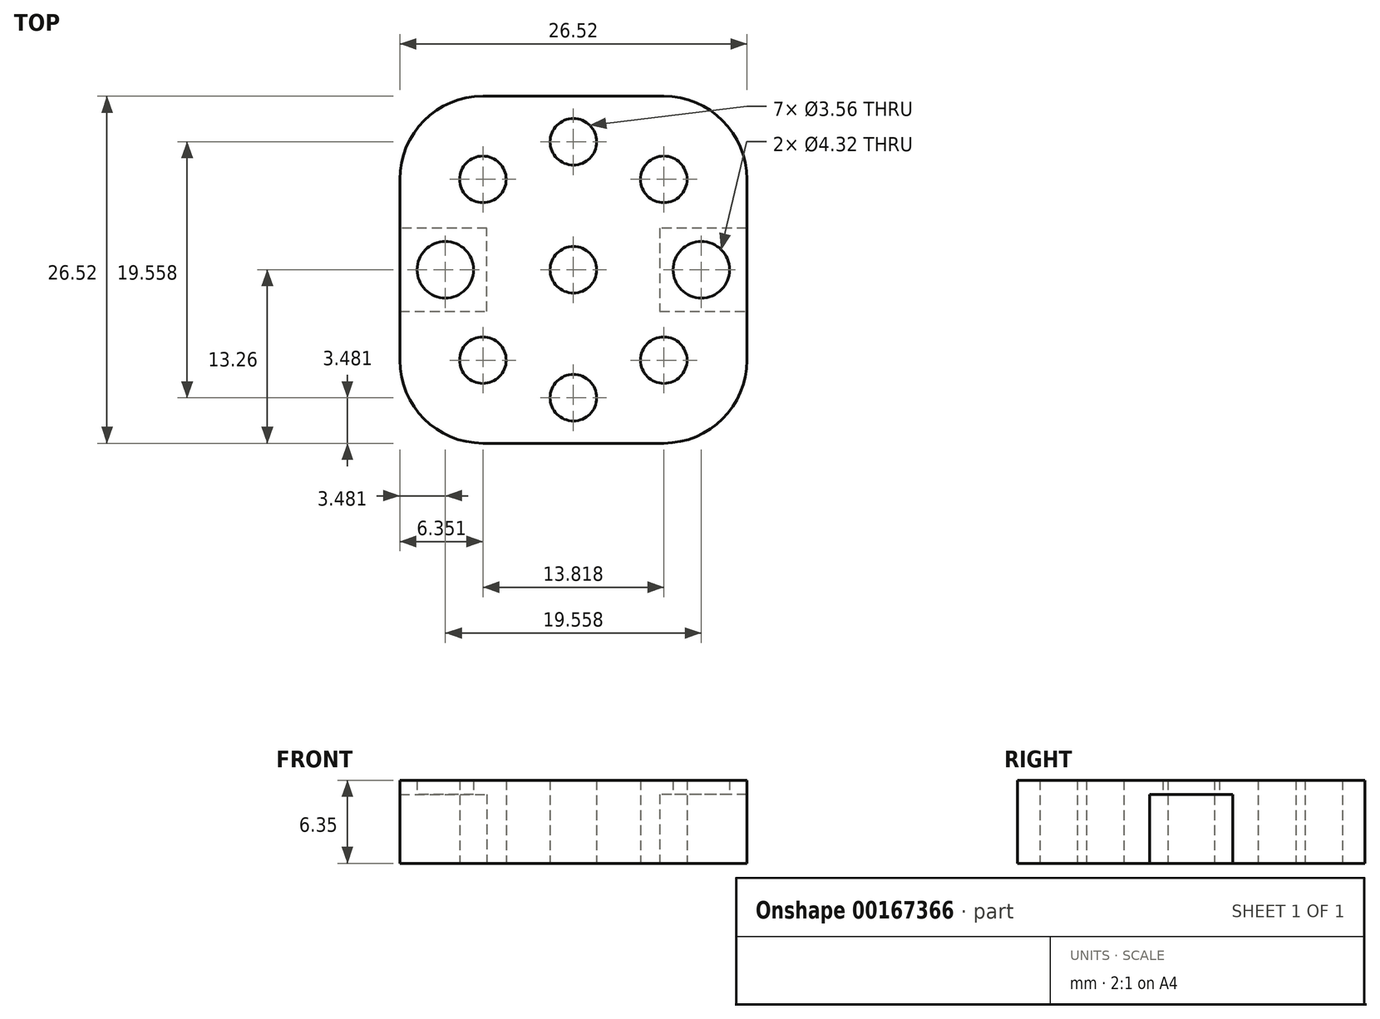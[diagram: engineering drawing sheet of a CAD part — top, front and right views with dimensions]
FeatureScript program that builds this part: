
annotation { "Feature Type Name" : "Feature", "Feature Type Description" : "" }
export const myFeature = defineFeature(function(context is Context, id is Id, definition is map)
    precondition{}
    {
        {
            var Q0;
            Q0=qCreatedBy(makeId("Top.planeOp"),FACE);
            var sketch = newSketch(context, id + "F0", { "sketchPlane" : qUnion([Q0])});
            skLineSegment(sketch, "E0.bottom", {"start": v(6.9, 13.26) * mm, "end": v(-6.9, 13.26) * mm});
            skLineSegment(sketch, "E0.top", {"start": v(6.9, -13.26) * mm, "end": v(-6.9, -13.26) * mm});
            skLineSegment(sketch, "E0.left", {"start": v(13.26, 6.9) * mm, "end": v(13.26, -6.9) * mm});
            skLineSegment(sketch, "E0.right", {"start": v(-13.26, 6.9) * mm, "end": v(-13.26, -6.9) * mm});
            skPoint(sketch, "E0.middle", {"position": v(0, 0) * mm});
            skCircle(sketch, "E1", {"center": v(0, 0) * mm, "radius": 1.78 * mm});
            skCircle(sketch, "E2", {"center": v(-6.9, 6.9) * mm, "radius": 1.78 * mm});
            skCircle(sketch, "E3", {"center": v(-9.78, 0) * mm, "radius": 2.16 * mm});
            skCircle(sketch, "E4", {"center": v(-6.9, -6.9) * mm, "radius": 1.78 * mm});
            skCircle(sketch, "E5", {"center": v(6.9, -6.9) * mm, "radius": 1.78 * mm});
            skCircle(sketch, "E6", {"center": v(9.78, 0) * mm, "radius": 2.16 * mm});
            skCircle(sketch, "E7", {"center": v(6.9, 6.9) * mm, "radius": 1.78 * mm});
            skLineSegment(sketch, "E8", {"start": v(-6.9, 6.9) * mm, "end": v(6.9, 6.9) * mm, "construction": true});
            skLineSegment(sketch, "E9", {"start": v(6.9, -6.9) * mm, "end": v(-6.9, -6.9) * mm, "construction": true});
            skLineSegment(sketch, "E10", {"start": v(-6.9, -6.9) * mm, "end": v(-6.9, 6.9) * mm, "construction": true});
            skLineSegment(sketch, "E11", {"start": v(6.9, 6.9) * mm, "end": v(6.9, -6.9) * mm, "construction": true});
            skLineSegment(sketch, "E12", {"start": v(-6.9, -6.9) * mm, "end": v(6.9, 6.9) * mm, "construction": true});
            skLineSegment(sketch, "E13", {"start": v(0, 13.26) * mm, "end": v(0, -13.26) * mm, "construction": true});
            skCircle(sketch, "E14", {"center": v(0, 9.78) * mm, "radius": 1.78 * mm});
            skCircle(sketch, "E15", {"center": v(0, -9.78) * mm, "radius": 1.78 * mm});
            skPoint(sketch, "E16.visualSharp", {"position": v(-13.26, 13.26) * mm});
            skArc(sketch, "E16.filletArc", {"start": v(-6.9, 13.26) * mm, "mid": v(-11.4, 11.4) * mm, "end": v(-13.26, 6.9) * mm});
            skPoint(sketch, "E17.visualSharp", {"position": v(13.26, 13.26) * mm});
            skArc(sketch, "E17.filletArc", {"start": v(13.26, 6.9) * mm, "mid": v(11.4, 11.4) * mm, "end": v(6.9, 13.26) * mm});
            skPoint(sketch, "E18.visualSharp", {"position": v(13.26, -13.26) * mm});
            skArc(sketch, "E18.filletArc", {"start": v(6.9, -13.26) * mm, "mid": v(11.4, -11.4) * mm, "end": v(13.26, -6.9) * mm});
            skPoint(sketch, "E19.visualSharp", {"position": v(-13.26, -13.26) * mm});
            skArc(sketch, "E19.filletArc", {"start": v(-13.26, -6.9) * mm, "mid": v(-11.4, -11.4) * mm, "end": v(-6.9, -13.26) * mm});
            skLineSegment(sketch, "E20", {"start": v(-13.26, 0) * mm, "end": v(13.26, 0) * mm, "construction": true});
            skLineSegment(sketch, "E21", {"start": v(-13.26, -3.18) * mm, "end": v(-6.6, -3.18) * mm});
            skLineSegment(sketch, "E22", {"start": v(-6.6, -3.18) * mm, "end": v(-6.6, 3.17) * mm});
            skLineSegment(sketch, "E23", {"start": v(-6.6, 3.17) * mm, "end": v(-13.26, 3.17) * mm});
            skLineSegment(sketch, "E24", {"start": v(13.26, 3.18) * mm, "end": v(6.6, 3.17) * mm});
            skLineSegment(sketch, "E25", {"start": v(6.6, 3.17) * mm, "end": v(6.6, -3.18) * mm});
            skLineSegment(sketch, "E26", {"start": v(6.6, -3.18) * mm, "end": v(13.26, -3.18) * mm});
            skSolve(sketch);
        }
        {
            var Q0;
            Q0 = qSketchRegion(id + "F0", true);
            extrude(context, id + "F1", {"entities" : qUnion([Q0]), "depth" : 6.35 * mm});
        }
        {
            var Q0;
            Q0=makeQuery(id+"F0.imprint","IMPRINT",FACE,{"disambiguationData":[TD([[makeQuery(id+"F0.imprint","IMPRINT",EDGE,{"derivedFrom":sQuery(id+"F0.wireOp",EDGE,"E3")}),-1.0]])]});
            var Q1;
            Q1=makeQuery(id+"F0.imprint","IMPRINT",FACE,{"disambiguationData":[TD([[makeQuery(id+"F0.imprint","IMPRINT",EDGE,{"derivedFrom":sQuery(id+"F0.wireOp",EDGE,"E6")}),-1.0]])]});
            extrude(context, id + "F2", {"entities" : qUnion([Q0, Q1]), "operationType" : NewBodyOperationType.REMOVE, "depth" : 5.27 * mm});
        }
    });
